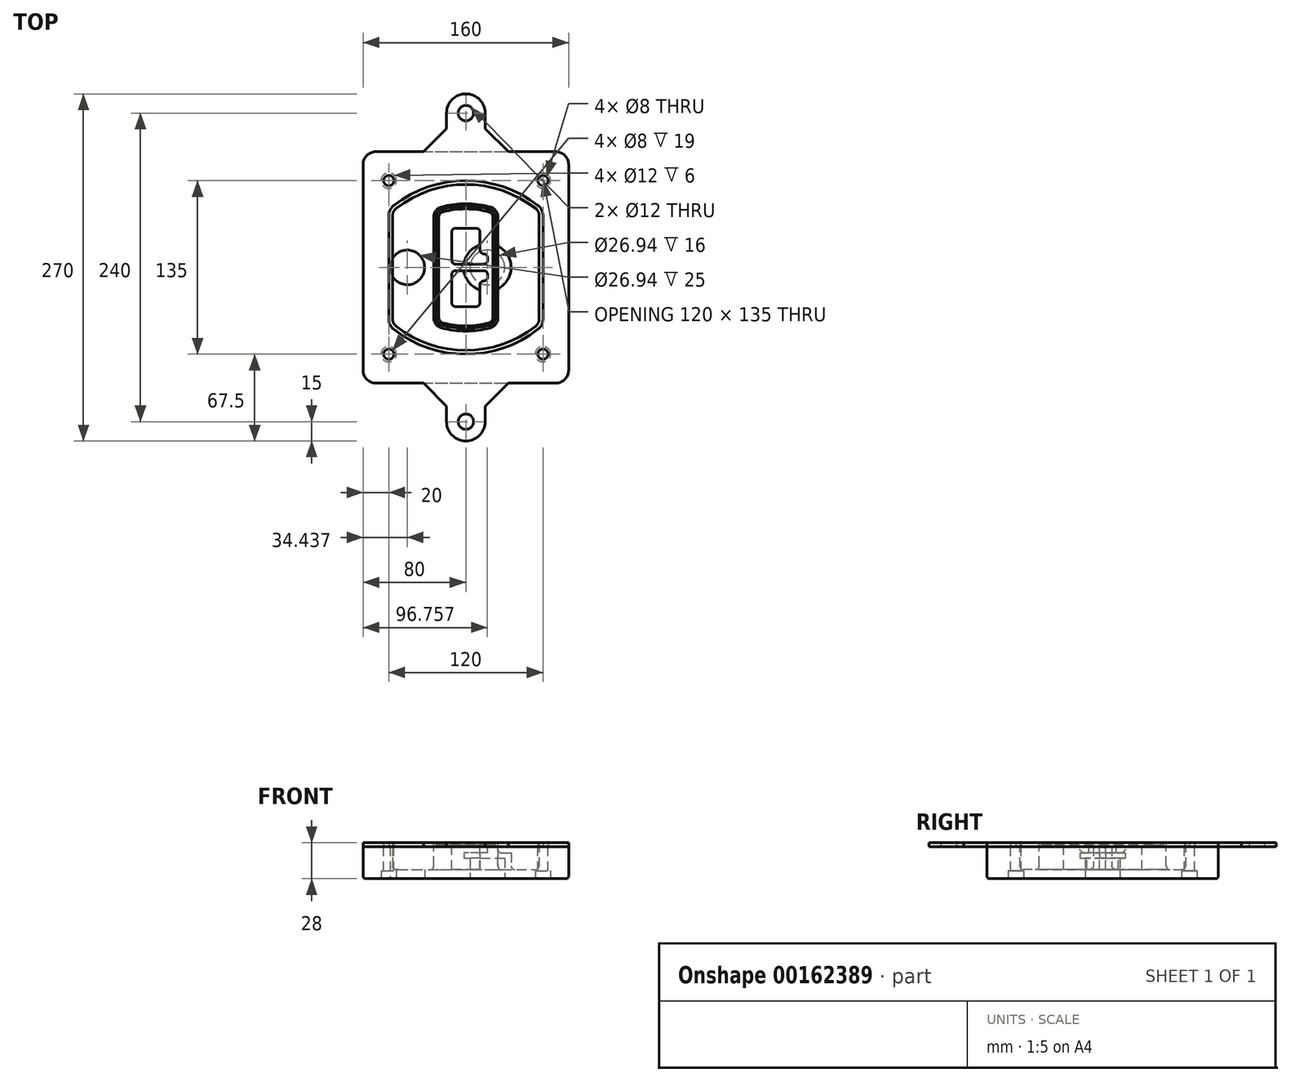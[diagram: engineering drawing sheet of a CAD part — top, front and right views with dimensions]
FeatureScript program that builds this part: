
annotation { "Feature Type Name" : "Feature", "Feature Type Description" : "" }
export const myFeature = defineFeature(function(context is Context, id is Id, definition is map)
    precondition{}
    {
        {
            var Q0;
            Q0=qCreatedBy(makeId("Top.planeOp"),FACE);
            var sketch = newSketch(context, id + "F0", { "sketchPlane" : qUnion([Q0])});
            skPoint(sketch, "E0.rect.middle", {"position": v(0, 0) * mm});
            skLineSegment(sketch, "E1.bottom", {"start": v(-70, -90) * mm, "end": v(70, -90) * mm});
            skLineSegment(sketch, "E1.top", {"start": v(-70, 90) * mm, "end": v(70, 90) * mm});
            skLineSegment(sketch, "E1.left", {"start": v(-80, -80) * mm, "end": v(-80, 80) * mm});
            skLineSegment(sketch, "E1.right", {"start": v(80, -80) * mm, "end": v(80, 80) * mm});
            skLineSegment(sketch, "E2", {"start": v(-80, 90) * mm, "end": v(80, -90) * mm, "construction": true});
            skLineSegment(sketch, "E3", {"start": v(80, 90) * mm, "end": v(-80, -90) * mm, "construction": true});
            skCircle(sketch, "E4", {"center": v(-60, 67.5) * mm, "radius": 4 * mm});
            skCircle(sketch, "E5", {"center": v(60, 67.5) * mm, "radius": 4 * mm});
            skCircle(sketch, "E6", {"center": v(60, -67.5) * mm, "radius": 4 * mm});
            skCircle(sketch, "E7", {"center": v(-60, -67.5) * mm, "radius": 4 * mm});
            skLineSegment(sketch, "E8", {"start": v(-60, 67.5) * mm, "end": v(60, 67.5) * mm, "construction": true});
            skLineSegment(sketch, "E9", {"start": v(60, 67.5) * mm, "end": v(60, -67.5) * mm, "construction": true});
            skLineSegment(sketch, "E10", {"start": v(60, -67.5) * mm, "end": v(-60, -67.5) * mm, "construction": true});
            skLineSegment(sketch, "E11", {"start": v(-60, -67.5) * mm, "end": v(-60, 67.5) * mm, "construction": true});
            skLineSegment(sketch, "E12", {"start": v(-60, 40.3) * mm, "end": v(-60, -40.3) * mm});
            skLineSegment(sketch, "E13", {"start": v(60, 40.3) * mm, "end": v(60, -40.3) * mm});
            skArc(sketch, "E14", {"start": v(56.15, 48.18) * mm, "mid": v(0, 67.5) * mm, "end": v(-56.15, 48.18) * mm});
            skArc(sketch, "E15", {"start": v(-56.15, -48.18) * mm, "mid": v(0, -67.5) * mm, "end": v(56.15, -48.18) * mm});
            skLineSegment(sketch, "E16", {"start": v(-60, 0) * mm, "end": v(60, 0) * mm, "construction": true});
            skPoint(sketch, "E17.visualSharp", {"position": v(-60, -45) * mm});
            skArc(sketch, "E17.filletArc", {"start": v(-60, -40.3) * mm, "mid": v(-58.99, -44.68) * mm, "end": v(-56.15, -48.18) * mm});
            skPoint(sketch, "E18.visualSharp", {"position": v(-60, 45) * mm});
            skArc(sketch, "E18.filletArc", {"start": v(-56.15, 48.18) * mm, "mid": v(-58.99, 44.68) * mm, "end": v(-60, 40.3) * mm});
            skPoint(sketch, "E19.visualSharp", {"position": v(60, 45) * mm});
            skArc(sketch, "E19.filletArc", {"start": v(60, 40.3) * mm, "mid": v(58.99, 44.68) * mm, "end": v(56.15, 48.18) * mm});
            skPoint(sketch, "E20.visualSharp", {"position": v(60, -45) * mm});
            skArc(sketch, "E20.filletArc", {"start": v(56.15, -48.18) * mm, "mid": v(58.99, -44.68) * mm, "end": v(60, -40.3) * mm});
            skPoint(sketch, "E21.visualSharp", {"position": v(-80, 90) * mm});
            skArc(sketch, "E21.filletArc", {"start": v(-70, 90) * mm, "mid": v(-77.07, 87.07) * mm, "end": v(-80, 80) * mm});
            skPoint(sketch, "E22.visualSharp", {"position": v(80, 90) * mm});
            skArc(sketch, "E22.filletArc", {"start": v(80, 80) * mm, "mid": v(77.07, 87.07) * mm, "end": v(70, 90) * mm});
            skPoint(sketch, "E23.visualSharp", {"position": v(80, -90) * mm});
            skArc(sketch, "E23.filletArc", {"start": v(70, -90) * mm, "mid": v(77.07, -87.07) * mm, "end": v(80, -80) * mm});
            skPoint(sketch, "E24.visualSharp", {"position": v(-80, -90) * mm});
            skArc(sketch, "E24.filletArc", {"start": v(-80, -80) * mm, "mid": v(-77.07, -87.07) * mm, "end": v(-70, -90) * mm});
            skArc(sketch, "E25.0", {"start": v(57, 40.3) * mm, "mid": v(56.3, 43.36) * mm, "end": v(54.3, 45.81) * mm});
            skLineSegment(sketch, "E25.1", {"start": v(57, 40.3) * mm, "end": v(57, -40.3) * mm});
            skArc(sketch, "E25.2", {"start": v(54.3, -45.81) * mm, "mid": v(56.3, -43.36) * mm, "end": v(57, -40.3) * mm});
            skArc(sketch, "E25.3", {"start": v(-54.3, -45.81) * mm, "mid": v(0, -64.5) * mm, "end": v(54.3, -45.81) * mm});
            skArc(sketch, "E25.4", {"start": v(-57, -40.3) * mm, "mid": v(-56.3, -43.36) * mm, "end": v(-54.3, -45.81) * mm});
            skArc(sketch, "E25.5", {"start": v(54.3, 45.81) * mm, "mid": v(0, 64.5) * mm, "end": v(-54.3, 45.81) * mm});
            skLineSegment(sketch, "E25.6", {"start": v(-57, 40.3) * mm, "end": v(-57, -40.3) * mm});
            skArc(sketch, "E25.7", {"start": v(-54.3, 45.81) * mm, "mid": v(-56.3, 43.36) * mm, "end": v(-57, 40.3) * mm});
            skArc(sketch, "E26.0", {"start": v(-58.62, 51.33) * mm, "mid": v(-62.58, 46.43) * mm, "end": v(-64, 40.3) * mm});
            skArc(sketch, "E26.1", {"start": v(58.62, 51.33) * mm, "mid": v(0, 71.5) * mm, "end": v(-58.62, 51.33) * mm});
            skArc(sketch, "E26.2", {"start": v(64, 40.3) * mm, "mid": v(62.58, 46.43) * mm, "end": v(58.62, 51.33) * mm});
            skLineSegment(sketch, "E26.3", {"start": v(64, 40.3) * mm, "end": v(64, -40.3) * mm});
            skArc(sketch, "E26.4", {"start": v(58.62, -51.33) * mm, "mid": v(62.58, -46.43) * mm, "end": v(64, -40.3) * mm});
            skLineSegment(sketch, "E26.5", {"start": v(-64, 40.3) * mm, "end": v(-64, -40.3) * mm});
            skArc(sketch, "E26.6", {"start": v(-58.62, -51.33) * mm, "mid": v(0, -71.5) * mm, "end": v(58.62, -51.33) * mm});
            skArc(sketch, "E26.7", {"start": v(-64, -40.3) * mm, "mid": v(-62.58, -46.43) * mm, "end": v(-58.62, -51.33) * mm});
            skSolve(sketch);
        }
        {
            var Q0;
            Q0=makeQuery(id+"F0.imprint","IMPRINT",FACE,{"disambiguationData":[TD([[makeQuery(id+"F0.imprint","IMPRINT",EDGE,{"derivedFrom":sQuery(id+"F0.wireOp",EDGE,"E1.bottom")}),1.0]])]});
            var Q1;
            Q1=makeQuery(id+"F0.imprint","IMPRINT",FACE,{"disambiguationData":[TD([[makeQuery(id+"F0.imprint","IMPRINT",EDGE,{"derivedFrom":sQuery(id+"F0.wireOp",EDGE,"E12")}),1.0]])]});
            var Q2;
            Q2=makeQuery(id+"F0.imprint","IMPRINT",FACE,{"disambiguationData":[TD([[makeQuery(id+"F0.imprint","IMPRINT",EDGE,{"derivedFrom":sQuery(id+"F0.wireOp",EDGE,"E25.0")}),1.0]])]});
            var Q3;
            Q3=makeQuery(id+"F0.imprint","IMPRINT",FACE,{"disambiguationData":[TD([[makeQuery(id+"F0.imprint","IMPRINT",EDGE,{"derivedFrom":sQuery(id+"F0.wireOp",EDGE,"E12")}),-1.0]])]});
            extrude(context, id + "F1", {"entities" : qUnion([Q0, Q1, Q2, Q3]), "oppositeDirection" : true, "depth" : 25 * mm});
        }
        {
            var Q0;
            Q0=makeQuery(id+"F0.imprint","IMPRINT",FACE,{"disambiguationData":[TD([[makeQuery(id+"F0.imprint","IMPRINT",EDGE,{"derivedFrom":sQuery(id+"F0.wireOp",EDGE,"E12")}),1.0]])]});
            extrude(context, id + "F2", {"entities" : qUnion([Q0]), "operationType" : NewBodyOperationType.ADD, "depth" : 3 * mm});
        }
        {
            var Q0;
            Q0=makeQuery(id+"F0.imprint","IMPRINT",FACE,{"disambiguationData":[TD([[makeQuery(id+"F0.imprint","IMPRINT",EDGE,{"derivedFrom":sQuery(id+"F0.wireOp",EDGE,"E25.0")}),1.0]])]});
            extrude(context, id + "F3", {"entities" : qUnion([Q0]), "operationType" : NewBodyOperationType.REMOVE, "oppositeDirection" : true, "depth" : 18 * mm});
        }
        {
            var Q0;
            Q0=makeQuery(id+"F2.opExtrude","CAP_FACE",FACE,{"disambiguationData":[OSD([sQuery(id+"F0.wireOp",EDGE,"E12"),sQuery(id+"F0.wireOp",EDGE,"E13"),sQuery(id+"F0.wireOp",EDGE,"E14"),sQuery(id+"F0.wireOp",EDGE,"E15"),sQuery(id+"F0.wireOp",EDGE,"E17.filletArc"),sQuery(id+"F0.wireOp",EDGE,"E18.filletArc"),sQuery(id+"F0.wireOp",EDGE,"E19.filletArc"),sQuery(id+"F0.wireOp",EDGE,"E20.filletArc"),sQuery(id+"F0.wireOp",EDGE,"E25.0"),sQuery(id+"F0.wireOp",EDGE,"E25.1"),sQuery(id+"F0.wireOp",EDGE,"E25.2"),sQuery(id+"F0.wireOp",EDGE,"E25.3"),sQuery(id+"F0.wireOp",EDGE,"E25.4"),sQuery(id+"F0.wireOp",EDGE,"E25.5"),sQuery(id+"F0.wireOp",EDGE,"E25.6"),sQuery(id+"F0.wireOp",EDGE,"E25.7")])],"isStart":false});
            var sketch = newSketch(context, id + "F4", { "sketchPlane" : qUnion([Q0])});
            skArc(sketch, "E27.0", {"start": v(-19.08, -46.97) * mm, "mid": v(0, -49.5) * mm, "end": v(19.08, -46.97) * mm});
            skArc(sketch, "E28.0", {"start": v(19.08, 46.97) * mm, "mid": v(0, 49.5) * mm, "end": v(-19.08, 46.97) * mm});
            skLineSegment(sketch, "E29", {"start": v(-25, 39.25) * mm, "end": v(-25, -39.25) * mm});
            skLineSegment(sketch, "E30", {"start": v(25, 39.25) * mm, "end": v(25, -39.25) * mm});
            skLineSegment(sketch, "E31", {"start": v(-25, 45.1) * mm, "end": v(25, 45.1) * mm, "construction": true});
            skLineSegment(sketch, "E32", {"start": v(-25, -45.1) * mm, "end": v(25, -45.1) * mm, "construction": true});
            skPoint(sketch, "E33.visualSharp", {"position": v(-25, 45.1) * mm});
            skArc(sketch, "E33.filletArc", {"start": v(-19.08, 46.97) * mm, "mid": v(-23.35, 44.11) * mm, "end": v(-25, 39.25) * mm});
            skPoint(sketch, "E34.visualSharp", {"position": v(25, 45.1) * mm});
            skArc(sketch, "E34.filletArc", {"start": v(25, 39.25) * mm, "mid": v(23.35, 44.11) * mm, "end": v(19.08, 46.97) * mm});
            skPoint(sketch, "E35.visualSharp", {"position": v(25, -45.1) * mm});
            skArc(sketch, "E35.filletArc", {"start": v(19.08, -46.97) * mm, "mid": v(23.35, -44.11) * mm, "end": v(25, -39.25) * mm});
            skPoint(sketch, "E36.visualSharp", {"position": v(-25, -45.1) * mm});
            skArc(sketch, "E36.filletArc", {"start": v(-25, -39.25) * mm, "mid": v(-23.35, -44.11) * mm, "end": v(-19.08, -46.97) * mm});
            skArc(sketch, "E37.0", {"start": v(54.3, 45.81) * mm, "mid": v(0, 64.5) * mm, "end": v(-54.3, 45.81) * mm});
            skArc(sketch, "E37.1", {"start": v(-54.3, 45.81) * mm, "mid": v(-56.3, 43.36) * mm, "end": v(-57, 40.3) * mm});
            skLineSegment(sketch, "E37.2", {"start": v(-57, 40.3) * mm, "end": v(-57, -40.3) * mm});
            skArc(sketch, "E37.3", {"start": v(-57, -40.3) * mm, "mid": v(-56.3, -43.36) * mm, "end": v(-54.3, -45.81) * mm});
            skArc(sketch, "E37.4", {"start": v(-54.3, -45.81) * mm, "mid": v(0, -64.5) * mm, "end": v(54.3, -45.81) * mm});
            skArc(sketch, "E37.5", {"start": v(54.3, -45.81) * mm, "mid": v(56.3, -43.36) * mm, "end": v(57, -40.3) * mm});
            skLineSegment(sketch, "E37.6", {"start": v(57, 40.3) * mm, "end": v(57, -40.3) * mm});
            skArc(sketch, "E37.7", {"start": v(57, 40.3) * mm, "mid": v(56.3, 43.36) * mm, "end": v(54.3, 45.81) * mm});
            skLineSegment(sketch, "E38.0", {"start": v(23, 39.25) * mm, "end": v(23, -39.25) * mm});
            skArc(sketch, "E38.1", {"start": v(18.56, -45.04) * mm, "mid": v(21.76, -42.9) * mm, "end": v(23, -39.25) * mm});
            skArc(sketch, "E38.2", {"start": v(-18.56, -45.04) * mm, "mid": v(0, -47.5) * mm, "end": v(18.56, -45.04) * mm});
            skArc(sketch, "E38.3", {"start": v(-23, -39.25) * mm, "mid": v(-21.76, -42.9) * mm, "end": v(-18.56, -45.04) * mm});
            skLineSegment(sketch, "E38.4", {"start": v(-23, 39.25) * mm, "end": v(-23, -39.25) * mm});
            skArc(sketch, "E38.5", {"start": v(23, 39.25) * mm, "mid": v(21.76, 42.9) * mm, "end": v(18.56, 45.04) * mm});
            skArc(sketch, "E38.6", {"start": v(-18.56, 45.04) * mm, "mid": v(-21.76, 42.9) * mm, "end": v(-23, 39.25) * mm});
            skArc(sketch, "E38.7", {"start": v(18.56, 45.04) * mm, "mid": v(0, 47.5) * mm, "end": v(-18.56, 45.04) * mm});
            skArc(sketch, "E39.0", {"start": v(21, 39.25) * mm, "mid": v(20.18, 41.68) * mm, "end": v(18.04, 43.1) * mm});
            skLineSegment(sketch, "E39.1", {"start": v(21, 39.25) * mm, "end": v(21, -39.25) * mm});
            skArc(sketch, "E39.2", {"start": v(18.04, -43.1) * mm, "mid": v(20.18, -41.68) * mm, "end": v(21, -39.25) * mm});
            skArc(sketch, "E39.3", {"start": v(-18.04, -43.1) * mm, "mid": v(0, -45.5) * mm, "end": v(18.04, -43.1) * mm});
            skArc(sketch, "E39.4", {"start": v(-21, -39.25) * mm, "mid": v(-20.18, -41.68) * mm, "end": v(-18.04, -43.1) * mm});
            skArc(sketch, "E39.5", {"start": v(18.04, 43.1) * mm, "mid": v(0, 45.5) * mm, "end": v(-18.04, 43.1) * mm});
            skLineSegment(sketch, "E39.6", {"start": v(-21, 39.25) * mm, "end": v(-21, -39.25) * mm});
            skArc(sketch, "E39.7", {"start": v(-18.04, 43.1) * mm, "mid": v(-20.18, 41.68) * mm, "end": v(-21, 39.25) * mm});
            skLineSegment(sketch, "E40", {"start": v(-25, 0) * mm, "end": v(25, 0) * mm, "construction": true});
            skLineSegment(sketch, "E41", {"start": v(-11, 5.5) * mm, "end": v(-11, 27.5) * mm});
            skLineSegment(sketch, "E42", {"start": v(-8, 30.5) * mm, "end": v(8, 30.5) * mm});
            skLineSegment(sketch, "E43", {"start": v(11, 27.5) * mm, "end": v(11, 13.5) * mm});
            skLineSegment(sketch, "E44", {"start": v(14, 10.5) * mm, "end": v(14, 10.5) * mm});
            skLineSegment(sketch, "E45", {"start": v(17, 7.5) * mm, "end": v(17, 5.5) * mm});
            skLineSegment(sketch, "E46", {"start": v(14, 2.5) * mm, "end": v(-8, 2.5) * mm});
            skPoint(sketch, "E47.visualSharp", {"position": v(-11, 30.5) * mm});
            skArc(sketch, "E47.filletArc", {"start": v(-8, 30.5) * mm, "mid": v(-10.12, 29.62) * mm, "end": v(-11, 27.5) * mm});
            skPoint(sketch, "E48.visualSharp", {"position": v(11, 30.5) * mm});
            skArc(sketch, "E48.filletArc", {"start": v(11, 27.5) * mm, "mid": v(10.12, 29.62) * mm, "end": v(8, 30.5) * mm});
            skPoint(sketch, "E49.visualSharp", {"position": v(11, 10.5) * mm});
            skArc(sketch, "E49.filletArc", {"start": v(11, 13.5) * mm, "mid": v(11.88, 11.38) * mm, "end": v(14, 10.5) * mm});
            skPoint(sketch, "E50.visualSharp", {"position": v(17, 10.5) * mm});
            skArc(sketch, "E50.filletArc", {"start": v(17, 7.5) * mm, "mid": v(16.12, 9.62) * mm, "end": v(14, 10.5) * mm});
            skPoint(sketch, "E51.visualSharp", {"position": v(17, 2.5) * mm});
            skArc(sketch, "E51.filletArc", {"start": v(14, 2.5) * mm, "mid": v(16.12, 3.38) * mm, "end": v(17, 5.5) * mm});
            skPoint(sketch, "E52.visualSharp", {"position": v(-11, 2.5) * mm});
            skArc(sketch, "E52.filletArc", {"start": v(-11, 5.5) * mm, "mid": v(-10.12, 3.38) * mm, "end": v(-8, 2.5) * mm});
            skLineSegment(sketch, "E53.0.MirrorCS", {"start": v(14, -2.5) * mm, "end": v(-8, -2.5) * mm});
            skArc(sketch, "E54.0.MirrorCS", {"start": v(-11, -5.5) * mm, "mid": v(-10.12, -3.38) * mm, "end": v(-8, -2.5) * mm});
            skLineSegment(sketch, "E55.0.MirrorCS", {"start": v(-11, -5.5) * mm, "end": v(-11, -27.5) * mm});
            skArc(sketch, "E56.0.MirrorCS", {"start": v(-8, -30.5) * mm, "mid": v(-10.12, -29.62) * mm, "end": v(-11, -27.5) * mm});
            skLineSegment(sketch, "E57.0.MirrorCS", {"start": v(-8, -30.5) * mm, "end": v(8, -30.5) * mm});
            skArc(sketch, "E58.0.MirrorCS", {"start": v(11, -27.5) * mm, "mid": v(10.12, -29.62) * mm, "end": v(8, -30.5) * mm});
            skLineSegment(sketch, "E59.0.MirrorCS", {"start": v(11, -27.5) * mm, "end": v(11, -13.5) * mm});
            skArc(sketch, "E60.0.MirrorCS", {"start": v(11, -13.5) * mm, "mid": v(11.88, -11.38) * mm, "end": v(14, -10.5) * mm});
            skArc(sketch, "E61.0.MirrorCS", {"start": v(17, -7.5) * mm, "mid": v(16.12, -9.62) * mm, "end": v(14, -10.5) * mm});
            skLineSegment(sketch, "E62.0.MirrorCS", {"start": v(17, -7.5) * mm, "end": v(17, -5.5) * mm});
            skArc(sketch, "E63.0.MirrorCS", {"start": v(14, -2.5) * mm, "mid": v(16.12, -3.38) * mm, "end": v(17, -5.5) * mm});
            skSolve(sketch);
        }
        {
            var Q0;
            Q0=makeQuery(id+"F4.imprint","IMPRINT",FACE,{"disambiguationData":[TD([[makeQuery(id+"F4.imprint","IMPRINT",EDGE,{"derivedFrom":sQuery(id+"F4.wireOp",EDGE,"E27.0")}),1.0]])]});
            var Q1;
            Q1=makeQuery(id+"F4.imprint","IMPRINT",FACE,{"disambiguationData":[TD([[makeQuery(id+"F4.imprint","IMPRINT",EDGE,{"derivedFrom":sQuery(id+"F4.wireOp",EDGE,"E38.0")}),-1.0]])]});
            var Q2;
            Q2=makeQuery(id+"F4.imprint","IMPRINT",FACE,{"disambiguationData":[TD([[makeQuery(id+"F4.imprint","IMPRINT",EDGE,{"derivedFrom":sQuery(id+"F4.wireOp",EDGE,"E39.0")}),1.0]])]});
            extrude(context, id + "F5", {"entities" : qUnion([Q0, Q1, Q2]), "operationType" : NewBodyOperationType.ADD, "endBound" : BoundingType.UP_TO_NEXT, "oppositeDirection" : true, "depth" : 25 * mm});
        }
        {
            var Q0;
            Q0=makeQuery(id+"F4.imprint","IMPRINT",FACE,{"disambiguationData":[TD([[makeQuery(id+"F4.imprint","IMPRINT",EDGE,{"derivedFrom":sQuery(id+"F4.wireOp",EDGE,"E38.0")}),-1.0]])]});
            extrude(context, id + "F6", {"entities" : qUnion([Q0]), "operationType" : NewBodyOperationType.REMOVE, "oppositeDirection" : true, "depth" : 2 * mm});
        }
        {
            var Q0;
            Q0=makeQuery(id+"F1.opExtrude","CAP_FACE",FACE,{"disambiguationData":[OSD([sQuery(id+"F0.wireOp",EDGE,"E1.bottom"),sQuery(id+"F0.wireOp",EDGE,"E1.top"),sQuery(id+"F0.wireOp",EDGE,"E1.left"),sQuery(id+"F0.wireOp",EDGE,"E1.right"),sQuery(id+"F0.wireOp",EDGE,"E4"),sQuery(id+"F0.wireOp",EDGE,"E5"),sQuery(id+"F0.wireOp",EDGE,"E6"),sQuery(id+"F0.wireOp",EDGE,"E7"),sQuery(id+"F0.wireOp",EDGE,"E21.filletArc"),sQuery(id+"F0.wireOp",EDGE,"E22.filletArc"),sQuery(id+"F0.wireOp",EDGE,"E23.filletArc"),sQuery(id+"F0.wireOp",EDGE,"E24.filletArc")])],"isStart":false});
            var sketch = newSketch(context, id + "F7", { "sketchPlane" : qUnion([Q0])});
            skCircle(sketch, "E64", {"center": v(16.76, 0) * mm, "radius": 13.47 * mm});
            skCircle(sketch, "E65", {"center": v(-45.56, 0) * mm, "radius": 13.47 * mm});
            skLineSegment(sketch, "E66", {"start": v(80, 0) * mm, "end": v(-80, 0) * mm});
            skCircle(sketch, "E67", {"center": v(16.76, 0) * mm, "radius": 18.47 * mm});
            skCircle(sketch, "E68", {"center": v(60, -67.5) * mm, "radius": 6 * mm});
            skCircle(sketch, "E69", {"center": v(-60, -67.5) * mm, "radius": 6 * mm});
            skCircle(sketch, "E70", {"center": v(-60, 67.5) * mm, "radius": 6 * mm});
            skCircle(sketch, "E71", {"center": v(60, 67.5) * mm, "radius": 6 * mm});
            skSolve(sketch);
        }
        {
            var Q0;
            {var subQ1=sQuery(id+"F7.wireOp",EDGE,"E66");var subQ4=sQuery(id+"F7.wireOp",EDGE,"E64");var subQ6=makeQuery(id+"F7.imprint","INTERSECT",VERTEX,{"disambiguationData":[OD(0.0)],"derivedFrom":[subQ4,subQ1]});Q0=makeQuery(id+"F7.imprint","IMPRINT",FACE,{"disambiguationData":[TD([[makeQuery(id+"F7.imprint","IMPRINT",EDGE,{"disambiguationData":[TD([[subQ6,-1.0]])],"derivedFrom":subQ4}),-1.0]])]});}
            var Q1;
            {var subQ0=sQuery(id+"F7.wireOp",EDGE,"E66");var subQ1=sQuery(id+"F7.wireOp",EDGE,"E64");var subQ3=makeQuery(id+"F7.imprint","INTERSECT",VERTEX,{"disambiguationData":[OD(0.0)],"derivedFrom":[subQ1,subQ0]});Q1=makeQuery(id+"F7.imprint","IMPRINT",FACE,{"disambiguationData":[TD([[makeQuery(id+"F7.imprint","IMPRINT",EDGE,{"disambiguationData":[TD([[subQ3,-1.0]])],"derivedFrom":subQ1}),1.0]])]});}
            var Q2;
            {var subQ0=sQuery(id+"F7.wireOp",EDGE,"E66");var subQ1=sQuery(id+"F7.wireOp",EDGE,"E64");var subQ3=makeQuery(id+"F7.imprint","INTERSECT",VERTEX,{"disambiguationData":[OD(0.0)],"derivedFrom":[subQ1,subQ0]});Q2=makeQuery(id+"F7.imprint","IMPRINT",FACE,{"disambiguationData":[TD([[makeQuery(id+"F7.imprint","IMPRINT",EDGE,{"disambiguationData":[TD([[subQ3,1.0]])],"derivedFrom":subQ1}),1.0]])]});}
            var Q3;
            {var subQ1=sQuery(id+"F7.wireOp",EDGE,"E66");var subQ4=sQuery(id+"F7.wireOp",EDGE,"E64");var subQ6=makeQuery(id+"F7.imprint","INTERSECT",VERTEX,{"disambiguationData":[OD(0.0)],"derivedFrom":[subQ4,subQ1]});Q3=makeQuery(id+"F7.imprint","IMPRINT",FACE,{"disambiguationData":[TD([[makeQuery(id+"F7.imprint","IMPRINT",EDGE,{"disambiguationData":[TD([[subQ6,1.0]])],"derivedFrom":subQ4}),-1.0]])]});}
            extrude(context, id + "F8", {"entities" : qUnion([Q0, Q1, Q2, Q3]), "operationType" : NewBodyOperationType.ADD, "oppositeDirection" : true, "depth" : 20 * mm});
        }
        {
            var Q0;
            {var subQ0=sQuery(id+"F7.wireOp",EDGE,"E66");var subQ1=sQuery(id+"F7.wireOp",EDGE,"E64");var subQ3=makeQuery(id+"F7.imprint","INTERSECT",VERTEX,{"disambiguationData":[OD(0.0)],"derivedFrom":[subQ1,subQ0]});Q0=makeQuery(id+"F7.imprint","IMPRINT",FACE,{"disambiguationData":[TD([[makeQuery(id+"F7.imprint","IMPRINT",EDGE,{"disambiguationData":[TD([[subQ3,-1.0]])],"derivedFrom":subQ1}),1.0]])]});}
            var Q1;
            {var subQ0=sQuery(id+"F7.wireOp",EDGE,"E66");var subQ1=sQuery(id+"F7.wireOp",EDGE,"E64");var subQ3=makeQuery(id+"F7.imprint","INTERSECT",VERTEX,{"disambiguationData":[OD(0.0)],"derivedFrom":[subQ1,subQ0]});Q1=makeQuery(id+"F7.imprint","IMPRINT",FACE,{"disambiguationData":[TD([[makeQuery(id+"F7.imprint","IMPRINT",EDGE,{"disambiguationData":[TD([[subQ3,1.0]])],"derivedFrom":subQ1}),1.0]])]});}
            extrude(context, id + "F9", {"entities" : qUnion([Q0, Q1]), "operationType" : NewBodyOperationType.REMOVE, "oppositeDirection" : true, "depth" : 16 * mm});
        }
        {
            var Q0;
            {var subQ0=sQuery(id+"F7.wireOp",EDGE,"E66");var subQ1=sQuery(id+"F7.wireOp",EDGE,"E65");var subQ3=makeQuery(id+"F7.imprint","INTERSECT",VERTEX,{"disambiguationData":[OD(0.0)],"derivedFrom":[subQ1,subQ0]});Q0=makeQuery(id+"F7.imprint","IMPRINT",FACE,{"disambiguationData":[TD([[makeQuery(id+"F7.imprint","IMPRINT",EDGE,{"disambiguationData":[TD([[subQ3,-1.0]])],"derivedFrom":subQ1}),1.0]])]});}
            var Q1;
            {var subQ0=sQuery(id+"F7.wireOp",EDGE,"E66");var subQ1=sQuery(id+"F7.wireOp",EDGE,"E65");var subQ3=makeQuery(id+"F7.imprint","INTERSECT",VERTEX,{"disambiguationData":[OD(0.0)],"derivedFrom":[subQ1,subQ0]});Q1=makeQuery(id+"F7.imprint","IMPRINT",FACE,{"disambiguationData":[TD([[makeQuery(id+"F7.imprint","IMPRINT",EDGE,{"disambiguationData":[TD([[subQ3,1.0]])],"derivedFrom":subQ1}),1.0]])]});}
            extrude(context, id + "F10", {"entities" : qUnion([Q0, Q1]), "operationType" : NewBodyOperationType.REMOVE, "oppositeDirection" : true, "depth" : 25 * mm});
        }
        {
            var Q0;
            Q0=makeQuery(id+"F7.imprint","IMPRINT",FACE,{"disambiguationData":[TD([[makeQuery(id+"F7.imprint","IMPRINT",EDGE,{"derivedFrom":sQuery(id+"F7.wireOp",EDGE,"E68")}),1.0]])]});
            var Q1;
            Q1=makeQuery(id+"F7.imprint","IMPRINT",FACE,{"disambiguationData":[TD([[makeQuery(id+"F7.imprint","IMPRINT",EDGE,{"derivedFrom":makeQuery(id+"F1.opExtrude","CAP_EDGE",EDGE,{"disambiguationData":[OSD([sQuery(id+"F0.wireOp",EDGE,"E5")])],"isStart":false})}),-1.0]])]});
            var Q2;
            Q2=makeQuery(id+"F7.imprint","IMPRINT",FACE,{"disambiguationData":[TD([[makeQuery(id+"F7.imprint","IMPRINT",EDGE,{"derivedFrom":sQuery(id+"F7.wireOp",EDGE,"E69")}),1.0]])]});
            var Q3;
            Q3=makeQuery(id+"F7.imprint","IMPRINT",FACE,{"disambiguationData":[TD([[makeQuery(id+"F7.imprint","IMPRINT",EDGE,{"derivedFrom":makeQuery(id+"F1.opExtrude","CAP_EDGE",EDGE,{"disambiguationData":[OSD([sQuery(id+"F0.wireOp",EDGE,"E4")])],"isStart":false})}),-1.0]])]});
            var Q4;
            Q4=makeQuery(id+"F7.imprint","IMPRINT",FACE,{"disambiguationData":[TD([[makeQuery(id+"F7.imprint","IMPRINT",EDGE,{"derivedFrom":sQuery(id+"F7.wireOp",EDGE,"E70")}),1.0]])]});
            var Q5;
            Q5=makeQuery(id+"F7.imprint","IMPRINT",FACE,{"disambiguationData":[TD([[makeQuery(id+"F7.imprint","IMPRINT",EDGE,{"derivedFrom":makeQuery(id+"F1.opExtrude","CAP_EDGE",EDGE,{"disambiguationData":[OSD([sQuery(id+"F0.wireOp",EDGE,"E7")])],"isStart":false})}),-1.0]])]});
            var Q6;
            Q6=makeQuery(id+"F7.imprint","IMPRINT",FACE,{"disambiguationData":[TD([[makeQuery(id+"F7.imprint","IMPRINT",EDGE,{"derivedFrom":sQuery(id+"F7.wireOp",EDGE,"E71")}),1.0]])]});
            var Q7;
            Q7=makeQuery(id+"F7.imprint","IMPRINT",FACE,{"disambiguationData":[TD([[makeQuery(id+"F7.imprint","IMPRINT",EDGE,{"derivedFrom":makeQuery(id+"F1.opExtrude","CAP_EDGE",EDGE,{"disambiguationData":[OSD([sQuery(id+"F0.wireOp",EDGE,"E6")])],"isStart":false})}),-1.0]])]});
            extrude(context, id + "F11", {"entities" : qUnion([Q0, Q1, Q2, Q3, Q4, Q5, Q6, Q7]), "operationType" : NewBodyOperationType.REMOVE, "oppositeDirection" : true, "depth" : 6 * mm});
        }
        {
            var Q0;
            Q0=makeQuery(id+"F9.boolean.opBoolean","COPY",FACE,{"derivedFrom":makeQuery(id+"F9.opExtrude","CAP_FACE",FACE,{"disambiguationData":[OSD([sQuery(id+"F7.wireOp",EDGE,"E64")])],"isStart":false})});
            var sketch = newSketch(context, id + "F12", { "sketchPlane" : qUnion([Q0])});
            skArc(sketch, "E72.0", {"start": v(11, 17.55) * mm, "mid": v(2.57, 11.82) * mm, "end": v(-1.54, 2.5) * mm});
            skArc(sketch, "E72.1", {"start": v(-1.54, -2.5) * mm, "mid": v(2.57, -11.82) * mm, "end": v(11, -17.55) * mm});
            skLineSegment(sketch, "E73", {"start": v(-1.54, -2.5) * mm, "end": v(14, -2.5) * mm});
            skLineSegment(sketch, "E74.0", {"start": v(14, 2.5) * mm, "end": v(-1.54, 2.5) * mm});
            skArc(sketch, "E74.1", {"start": v(14, 2.5) * mm, "mid": v(16.12, 3.38) * mm, "end": v(17, 5.5) * mm});
            skLineSegment(sketch, "E74.2", {"start": v(17, 7.5) * mm, "end": v(17, 5.5) * mm});
            skArc(sketch, "E74.3", {"start": v(17, 7.5) * mm, "mid": v(16.12, 9.62) * mm, "end": v(14, 10.5) * mm});
            skArc(sketch, "E74.4", {"start": v(11, 13.5) * mm, "mid": v(11.88, 11.38) * mm, "end": v(14, 10.5) * mm});
            skLineSegment(sketch, "E74.5", {"start": v(11, 17.55) * mm, "end": v(11, 13.5) * mm});
            skLineSegment(sketch, "E74.7", {"start": v(14, -2.5) * mm, "end": v(-1.54, -2.5) * mm});
            skArc(sketch, "E74.8", {"start": v(14, -2.5) * mm, "mid": v(16.12, -3.38) * mm, "end": v(17, -5.5) * mm});
            skLineSegment(sketch, "E74.9", {"start": v(17, -7.5) * mm, "end": v(17, -5.5) * mm});
            skArc(sketch, "E74.10", {"start": v(17, -7.5) * mm, "mid": v(16.12, -9.62) * mm, "end": v(14, -10.5) * mm});
            skArc(sketch, "E74.11", {"start": v(11, -13.5) * mm, "mid": v(11.88, -11.38) * mm, "end": v(14, -10.5) * mm});
            skLineSegment(sketch, "E74.12", {"start": v(11, -17.55) * mm, "end": v(11, -13.5) * mm});
            skPoint(sketch, "E75.orphan", {"position": v(11, -27.5) * mm});
            skPoint(sketch, "E76.orphan", {"position": v(-8, -2.5) * mm});
            skPoint(sketch, "E77.orphan", {"position": v(-8, 2.5) * mm});
            skPoint(sketch, "E78.orphan", {"position": v(11, 27.5) * mm});
            skSolve(sketch);
        }
        {
            var Q0;
            {var subQ7=sQuery(id+"F12.wireOp",EDGE,"E72.0");var subQ14=sQuery(id+"F12.wireOp",EDGE,"E72.1");var subQ16=sQuery(id+"F12.wireOp",EDGE,"E74.1");var subQ18=sQuery(id+"F12.wireOp",EDGE,"E74.8");Q0=qUnion([makeQuery(id+"F12.imprint","IMPRINT",FACE,{"disambiguationData":[TD([[makeQuery(id+"F12.imprint","IMPRINT",EDGE,{"derivedFrom":subQ7}),1.0]])]}),makeQuery(id+"F12.imprint","IMPRINT",FACE,{"disambiguationData":[TD([[makeQuery(id+"F12.imprint","IMPRINT",EDGE,{"derivedFrom":subQ14}),1.0]])]}),makeQuery(id+"F12.imprint","IMPRINT",FACE,{"disambiguationData":[TD([[makeQuery(id+"F12.imprint","IMPRINT",EDGE,{"derivedFrom":subQ16}),1.0]])]}),makeQuery(id+"F12.imprint","IMPRINT",FACE,{"disambiguationData":[TD([[makeQuery(id+"F12.imprint","IMPRINT",EDGE,{"derivedFrom":subQ18}),-1.0]])]})]);}
            var Q1;
            Q1=makeQuery(id+"F5.boolean.opBoolean","SPLIT",FACE,{"disambiguationData":[TD([makeQuery(id+"F5.opExtrude","SWEPT_FACE",FACE,{"disambiguationData":[OSD([sQuery(id+"F4.wireOp",EDGE,"E41")])]})])],"derivedFrom":makeQuery(id+"F3.boolean.opBoolean","COPY",FACE,{"derivedFrom":makeQuery(id+"F3.opExtrude","CAP_FACE",FACE,{"disambiguationData":[OSD([sQuery(id+"F0.wireOp",EDGE,"E25.0"),sQuery(id+"F0.wireOp",EDGE,"E25.1"),sQuery(id+"F0.wireOp",EDGE,"E25.2"),sQuery(id+"F0.wireOp",EDGE,"E25.3"),sQuery(id+"F0.wireOp",EDGE,"E25.4"),sQuery(id+"F0.wireOp",EDGE,"E25.5"),sQuery(id+"F0.wireOp",EDGE,"E25.6"),sQuery(id+"F0.wireOp",EDGE,"E25.7")])],"isStart":false})})});
            extrude(context, id + "F13", {"entities" : qUnion([Q0]), "operationType" : NewBodyOperationType.REMOVE, "endBound" : BoundingType.UP_TO_SURFACE, "endBoundEntityFace" : qUnion([Q1]), "depth" : 25 * mm});
        }
        {
            var Q0;
            Q0=makeQuery(id+"F3.boolean.opBoolean","COPY",EDGE,{"derivedFrom":makeQuery(id+"F3.opExtrude","CAP_EDGE",EDGE,{"disambiguationData":[OSD([sQuery(id+"F0.wireOp",EDGE,"E25.6")])],"isStart":false})});
            var Q1;
            Q1=makeQuery(id+"F8.boolean.opBoolean","INTERSECT",EDGE,{"derivedFrom":[makeQuery(id+"F5.opExtrude","SWEPT_FACE",FACE,{"disambiguationData":[OSD([sQuery(id+"F4.wireOp",EDGE,"E30")])]}),makeQuery(id+"F8.opExtrude","CAP_FACE",FACE,{"disambiguationData":[OSD([sQuery(id+"F7.wireOp",EDGE,"E67")])],"isStart":false})]});
            var Q2;
            Q2=makeQuery(id+"F8.boolean.opBoolean","INTERSECT",EDGE,{"disambiguationData":[OD(1.0)],"derivedFrom":[makeQuery(id+"F5.opExtrude","SWEPT_FACE",FACE,{"disambiguationData":[OSD([sQuery(id+"F4.wireOp",EDGE,"E30")])]}),makeQuery(id+"F8.opExtrude","SWEPT_FACE",FACE,{"disambiguationData":[OSD([sQuery(id+"F7.wireOp",EDGE,"E67")])]})]});
            var Q3;
            {var subQ0=sQuery(id+"F4.wireOp",EDGE,"E30");Q3=makeQuery(id+"F8.boolean.opBoolean","SPLIT",EDGE,{"disambiguationData":[TD([makeQuery(id+"F5.opExtrude","SWEPT_FACE",FACE,{"disambiguationData":[OSD([sQuery(id+"F4.wireOp",EDGE,"E35.filletArc")])]})])],"derivedFrom":makeQuery(id+"F5.opExtrude","CAP_EDGE",EDGE,{"disambiguationData":[OSD([subQ0])],"isStart":false})});}
            var Q4;
            {var subQ0=sQuery(id+"F0.wireOp",EDGE,"E25.7");var subQ1=sQuery(id+"F0.wireOp",EDGE,"E25.1");var subQ2=sQuery(id+"F0.wireOp",EDGE,"E25.6");var subQ3=sQuery(id+"F0.wireOp",EDGE,"E25.5");var subQ4=sQuery(id+"F0.wireOp",EDGE,"E25.4");var subQ5=sQuery(id+"F0.wireOp",EDGE,"E25.0");var subQ6=sQuery(id+"F0.wireOp",EDGE,"E25.2");var subQ7=sQuery(id+"F0.wireOp",EDGE,"E25.3");Q4=makeQuery(id+"F8.boolean.opBoolean","INTERSECT",EDGE,{"derivedFrom":[makeQuery(id+"F5.boolean.opBoolean","SPLIT",FACE,{"disambiguationData":[TD([makeQuery(id+"F2.opExtrude","SWEPT_FACE",FACE,{"disambiguationData":[OSD([subQ5])]})])],"derivedFrom":makeQuery(id+"F3.boolean.opBoolean","COPY",FACE,{"derivedFrom":makeQuery(id+"F3.opExtrude","CAP_FACE",FACE,{"disambiguationData":[OSD([subQ5,subQ1,subQ6,subQ7,subQ4,subQ3,subQ2,subQ0])],"isStart":false})})}),makeQuery(id+"F8.opExtrude","SWEPT_FACE",FACE,{"disambiguationData":[OSD([sQuery(id+"F7.wireOp",EDGE,"E67")])]})]});}
            var Q5;
            Q5=makeQuery(id+"F8.boolean.opBoolean","INTERSECT",EDGE,{"disambiguationData":[OD(0.0)],"derivedFrom":[makeQuery(id+"F5.opExtrude","SWEPT_FACE",FACE,{"disambiguationData":[OSD([sQuery(id+"F4.wireOp",EDGE,"E30")])]}),makeQuery(id+"F8.opExtrude","SWEPT_FACE",FACE,{"disambiguationData":[OSD([sQuery(id+"F7.wireOp",EDGE,"E67")])]})]});
            fillet(context, id + "F14", {"entities" : qUnion([Q0, Q1, Q2, Q3, Q4, Q5]), "radius" : 3 * mm, "tangentPropagation" : true, "allowEdgeOverflow" : false});
        }
        {
            var Q0;
            Q0=makeQuery(id+"F1.opExtrude","CAP_EDGE",EDGE,{"disambiguationData":[OSD([sQuery(id+"F0.wireOp",EDGE,"E1.bottom")])],"isStart":false});
            fillet(context, id + "F15", {"entities" : qUnion([Q0]), "radius" : 2 * mm, "tangentPropagation" : true, "allowEdgeOverflow" : false});
        }
        {
            var Q0;
            {var subQ0=sQuery(id+"F0.wireOp",EDGE,"E22.filletArc");var subQ1=sQuery(id+"F0.wireOp",EDGE,"E7");var subQ2=sQuery(id+"F0.wireOp",EDGE,"E6");var subQ3=sQuery(id+"F0.wireOp",EDGE,"E5");var subQ4=sQuery(id+"F0.wireOp",EDGE,"E4");var subQ5=sQuery(id+"F0.wireOp",EDGE,"E1.bottom");var subQ6=sQuery(id+"F0.wireOp",EDGE,"E21.filletArc");var subQ7=sQuery(id+"F0.wireOp",EDGE,"E1.top");var subQ8=sQuery(id+"F0.wireOp",EDGE,"E1.left");var subQ9=sQuery(id+"F0.wireOp",EDGE,"E1.right");var subQ10=sQuery(id+"F0.wireOp",EDGE,"E23.filletArc");var subQ11=sQuery(id+"F0.wireOp",EDGE,"E24.filletArc");Q0=makeQuery(id+"F2.boolean.opBoolean","SPLIT",FACE,{"disambiguationData":[TD([makeQuery(id+"F1.opExtrude","SWEPT_FACE",FACE,{"disambiguationData":[OSD([subQ5])]})])],"derivedFrom":makeQuery(id+"F1.opExtrude","CAP_FACE",FACE,{"disambiguationData":[OSD([subQ5,subQ7,subQ8,subQ9,subQ4,subQ3,subQ2,subQ1,subQ6,subQ0,subQ10,subQ11])],"isStart":true})});}
            var sketch = newSketch(context, id + "F16", { "sketchPlane" : qUnion([Q0])});
            skLineSegment(sketch, "E79.0", {"start": v(-70, 90) * mm, "end": v(70, 90) * mm});
            skArc(sketch, "E80.0", {"start": v(80, 80) * mm, "mid": v(77.07, 87.07) * mm, "end": v(70, 90) * mm});
            skLineSegment(sketch, "E81.0", {"start": v(80, -80) * mm, "end": v(80, 80) * mm});
            skArc(sketch, "E82.0", {"start": v(70, -90) * mm, "mid": v(77.07, -87.07) * mm, "end": v(80, -80) * mm});
            skLineSegment(sketch, "E83.0", {"start": v(-70, -90) * mm, "end": v(70, -90) * mm});
            skArc(sketch, "E84.0", {"start": v(-80, -80) * mm, "mid": v(-77.07, -87.07) * mm, "end": v(-70, -90) * mm});
            skLineSegment(sketch, "E85.0", {"start": v(-80, -80) * mm, "end": v(-80, 80) * mm});
            skLineSegment(sketch, "E86.0.5", {"start": v(70, 90) * mm, "end": v(-70, 90) * mm});
            skArc(sketch, "E86.0.6", {"start": v(-70, 90) * mm, "mid": v(-77.07, 87.07) * mm, "end": v(-80, 80) * mm});
            skLineSegment(sketch, "E86.0.7", {"start": v(-80, 80) * mm, "end": v(-80, -80) * mm});
            skCircle(sketch, "E87.0", {"center": v(-60, 67.5) * mm, "radius": 4 * mm});
            skCircle(sketch, "E88.0", {"center": v(60, 67.5) * mm, "radius": 4 * mm});
            skCircle(sketch, "E89.0", {"center": v(60, -67.5) * mm, "radius": 4 * mm});
            skArc(sketch, "E90.0", {"start": v(56.15, -48.18) * mm, "mid": v(58.99, -44.68) * mm, "end": v(60, -40.3) * mm});
            skLineSegment(sketch, "E91.0", {"start": v(60, 40.3) * mm, "end": v(60, -40.3) * mm});
            skArc(sketch, "E92.0", {"start": v(60, 40.3) * mm, "mid": v(58.99, 44.68) * mm, "end": v(56.15, 48.18) * mm});
            skArc(sketch, "E93.0", {"start": v(56.15, 48.18) * mm, "mid": v(0, 67.5) * mm, "end": v(-56.15, 48.18) * mm});
            skArc(sketch, "E94.0", {"start": v(-56.15, 48.18) * mm, "mid": v(-58.99, 44.68) * mm, "end": v(-60, 40.3) * mm});
            skLineSegment(sketch, "E95.0", {"start": v(-60, 40.3) * mm, "end": v(-60, -40.3) * mm});
            skArc(sketch, "E96.0", {"start": v(-60, -40.3) * mm, "mid": v(-58.99, -44.68) * mm, "end": v(-56.15, -48.18) * mm});
            skArc(sketch, "E97.0", {"start": v(-56.15, -48.18) * mm, "mid": v(0, -67.5) * mm, "end": v(56.15, -48.18) * mm});
            skCircle(sketch, "E98.0", {"center": v(-60, -67.5) * mm, "radius": 4 * mm});
            skLineSegment(sketch, "E99", {"start": v(0, 23.75) * mm, "end": v(0, 120) * mm, "construction": true});
            skPoint(sketch, "E99.endSnap0", {"position": v(0, 90) * mm});
            skCircle(sketch, "E100", {"center": v(0, 120) * mm, "radius": 6 * mm});
            skLineSegment(sketch, "E101", {"start": v(-33, 90) * mm, "end": v(-15, 108) * mm});
            skLineSegment(sketch, "E102", {"start": v(-15, 108) * mm, "end": v(-15, 120) * mm});
            skArc(sketch, "E103", {"start": v(-15, 120) * mm, "mid": v(0, 135) * mm, "end": v(15, 120) * mm});
            skLineSegment(sketch, "E104", {"start": v(15, 120) * mm, "end": v(15, 108) * mm});
            skLineSegment(sketch, "E105", {"start": v(15, 108) * mm, "end": v(33, 90) * mm});
            skLineSegment(sketch, "E106", {"start": v(-80, 0) * mm, "end": v(80, 0) * mm, "construction": true});
            skCircle(sketch, "E107.MirrorC", {"center": v(0, -120) * mm, "radius": 6 * mm});
            skLineSegment(sketch, "E108.MirrorCS", {"start": v(-15, -108) * mm, "end": v(-15, -120) * mm});
            skLineSegment(sketch, "E109.MirrorCS", {"start": v(15, -120) * mm, "end": v(15, -108) * mm});
            skArc(sketch, "E110.MirrorCS", {"start": v(-15, -120) * mm, "mid": v(0, -135) * mm, "end": v(15, -120) * mm});
            skLineSegment(sketch, "E111.MirrorCS", {"start": v(-33, -90) * mm, "end": v(-15, -108) * mm});
            skLineSegment(sketch, "E112.MirrorCS", {"start": v(15, -108) * mm, "end": v(33, -90) * mm});
            skLineSegment(sketch, "E113.MirrorCS", {"start": v(0, -23.75) * mm, "end": v(0, -120) * mm, "construction": true});
            skSolve(sketch);
        }
        {
            var Q0;
            Q0 = qSketchRegion(id + "F16", true);
            var Q1;
            Q1=makeQuery(id+"F2.opExtrude","CAP_FACE",FACE,{"disambiguationData":[OSD([sQuery(id+"F0.wireOp",EDGE,"E12"),sQuery(id+"F0.wireOp",EDGE,"E13"),sQuery(id+"F0.wireOp",EDGE,"E14"),sQuery(id+"F0.wireOp",EDGE,"E15"),sQuery(id+"F0.wireOp",EDGE,"E17.filletArc"),sQuery(id+"F0.wireOp",EDGE,"E18.filletArc"),sQuery(id+"F0.wireOp",EDGE,"E19.filletArc"),sQuery(id+"F0.wireOp",EDGE,"E20.filletArc"),sQuery(id+"F0.wireOp",EDGE,"E25.0"),sQuery(id+"F0.wireOp",EDGE,"E25.1"),sQuery(id+"F0.wireOp",EDGE,"E25.2"),sQuery(id+"F0.wireOp",EDGE,"E25.3"),sQuery(id+"F0.wireOp",EDGE,"E25.4"),sQuery(id+"F0.wireOp",EDGE,"E25.5"),sQuery(id+"F0.wireOp",EDGE,"E25.6"),sQuery(id+"F0.wireOp",EDGE,"E25.7")])],"isStart":false});
            extrude(context, id + "F17", {"entities" : qUnion([Q0]), "endBound" : BoundingType.UP_TO_SURFACE, "endBoundEntityFace" : qUnion([Q1]), "depth" : 25 * mm});
        }
    });
